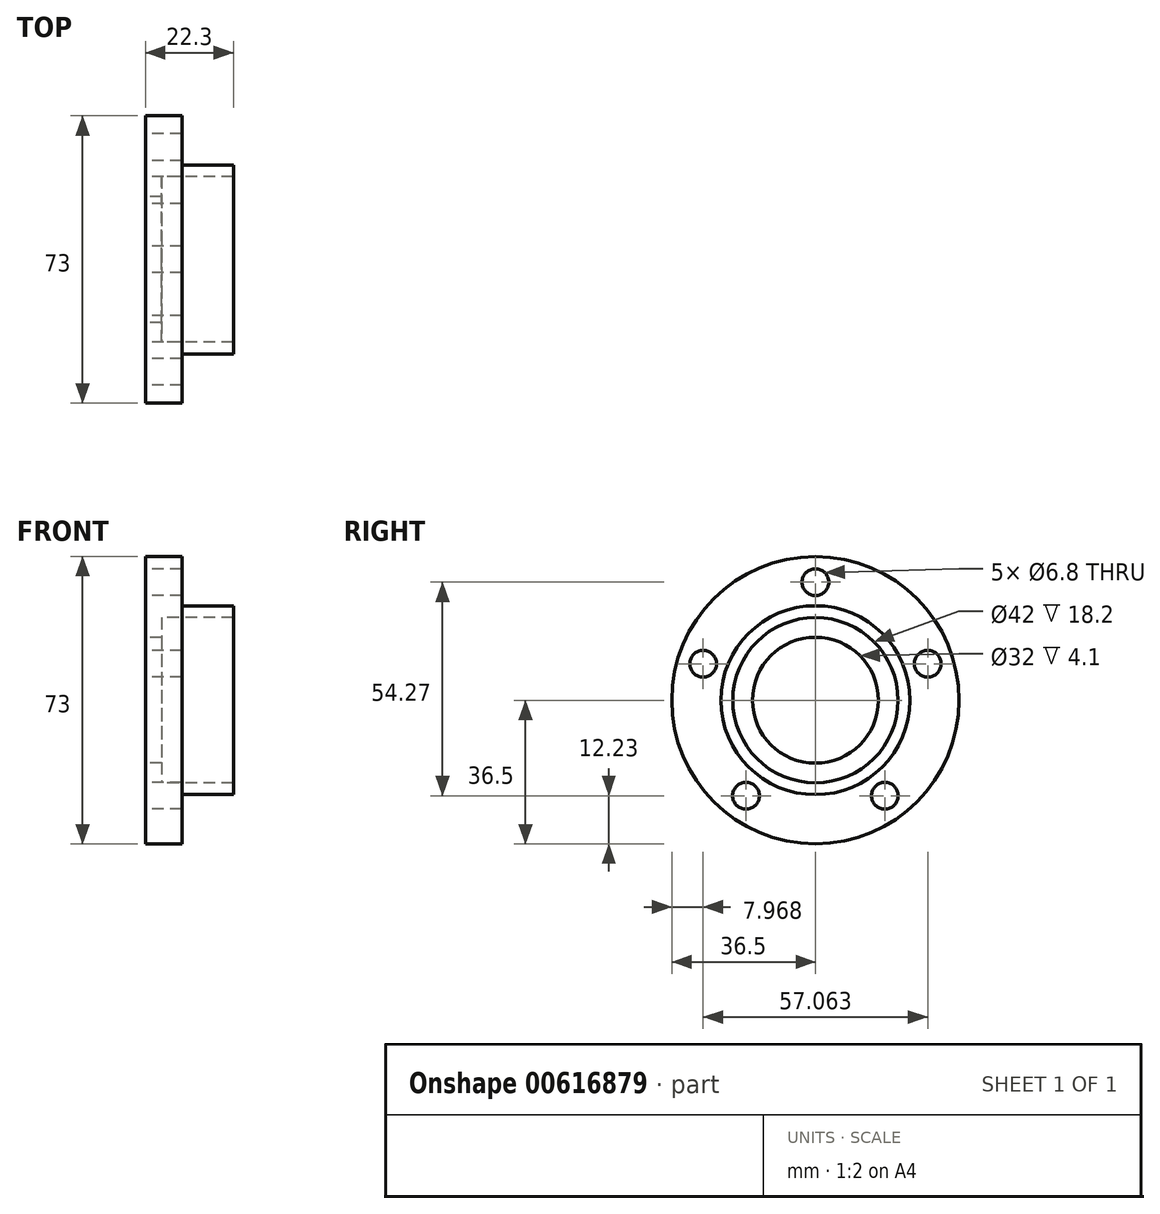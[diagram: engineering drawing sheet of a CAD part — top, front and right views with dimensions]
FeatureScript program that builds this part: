
annotation { "Feature Type Name" : "Feature", "Feature Type Description" : "" }
export const myFeature = defineFeature(function(context is Context, id is Id, definition is map)
    precondition{}
    {
        {
            var Q0;
            Q0=qCreatedBy(makeId("Front.planeOp"),FACE);
            var sketch = newSketch(context, id + "F0", { "sketchPlane" : qUnion([Q0])});
            skLineSegment(sketch, "E0", {"start": v(5.8, 21) * mm, "end": v(24, 21) * mm});
            skLineSegment(sketch, "E1", {"start": v(24, 24) * mm, "end": v(10.9, 24) * mm});
            skLineSegment(sketch, "E2", {"start": v(10.9, 24) * mm, "end": v(10.9, 36.5) * mm});
            skLineSegment(sketch, "E3", {"start": v(10.9, 36.5) * mm, "end": v(1.7, 36.5) * mm});
            skLineSegment(sketch, "E4", {"start": v(5.8, 21) * mm, "end": v(5.8, 16) * mm});
            skLineSegment(sketch, "E5", {"start": v(5.8, 16) * mm, "end": v(1.7, 16) * mm});
            skLineSegment(sketch, "E6", {"start": v(0, 0) * mm, "end": v(36.89, 0) * mm, "construction": true});
            skLineSegment(sketch, "E7", {"start": v(24, 21) * mm, "end": v(24, 24) * mm});
            skLineSegment(sketch, "E8", {"start": v(1.7, 16) * mm, "end": v(1.7, 36.5) * mm});
            skSolve(sketch);
        }
        {
            var Q0;
            Q0=makeQuery(id+"F0.imprint","IMPRINT",FACE,{"disambiguationData":[TD([[makeQuery(id+"F0.imprint","IMPRINT",EDGE,{"derivedFrom":sQuery(id+"F0.wireOp",EDGE,"E0")}),1.0]])]});
            var Q1;
            Q1=sQuery(id+"F0.wireOp",EDGE,"E6");
            revolve(context, id + "F1", {"surfaceOperationType" : NewSurfaceOperationType.NEW, "entities" : qUnion([Q0]), "axis" : qUnion([Q1]), "revolveType" : RevolveType.FULL});
        }
        {
            var Q0;
            Q0=makeQuery(id+"F1.opRevolve","SWEPT_FACE",FACE,{"disambiguationData":[OSD([sQuery(id+"F0.wireOp",EDGE,"E2")])]});
            var sketch = newSketch(context, id + "F2", { "sketchPlane" : qUnion([Q0])});
            skCircle(sketch, "E9.0", {"center": v(0, 0) * mm, "radius": 36.5 * mm, "construction": true});
            skCircle(sketch, "E10.0", {"center": v(0, 0) * mm, "radius": 24 * mm, "construction": true});
            skCircle(sketch, "E11", {"center": v(0, 0) * mm, "radius": 30 * mm, "construction": true});
            skCircle(sketch, "E12", {"center": v(0, 30) * mm, "radius": 2.5 * mm, "construction": true});
            skCircle(sketch, "E13.1.0", {"center": v(-28.53, 9.27) * mm, "radius": 2.5 * mm, "construction": true});
            skCircle(sketch, "E13.2.0", {"center": v(-17.63, -24.27) * mm, "radius": 2.5 * mm, "construction": true});
            skCircle(sketch, "E13.3.0", {"center": v(17.63, -24.27) * mm, "radius": 2.5 * mm, "construction": true});
            skCircle(sketch, "E13.4.0", {"center": v(28.53, 9.27) * mm, "radius": 2.5 * mm, "construction": true});
            skSolve(sketch);
        }
        {
            var Q0;
            Q0=sQuery(id+"F2.wireOp",VERTEX,"E12.center");
            var Q1;
            Q1=sQuery(id+"F2.wireOp",VERTEX,"E13.4.0.center");
            var Q2;
            Q2=sQuery(id+"F2.wireOp",VERTEX,"E13.3.0.center");
            var Q3;
            Q3=sQuery(id+"F2.wireOp",VERTEX,"E13.2.0.center");
            var Q4;
            Q4=sQuery(id+"F2.wireOp",VERTEX,"E13.1.0.center");
            var Q5;
            Q5=makeQuery(id+"F1.opRevolve","SWEPT_BODY",BODY,{"disambiguationData":[OSD([sQuery(id+"F0.wireOp",EDGE,"E0"),sQuery(id+"F0.wireOp",EDGE,"OTkLGTA6-KaCv-k9Gx-gSGP-BNMddn67J8YU"),sQuery(id+"F0.wireOp",EDGE,"E1"),sQuery(id+"F0.wireOp",EDGE,"dEY0dlj1-HALh-Q35b-Qvuc-SWXWftyWZpDn"),sQuery(id+"F0.wireOp",EDGE,"E2"),sQuery(id+"F0.wireOp",EDGE,"E3"),sQuery(id+"F0.wireOp",EDGE,"qeZPi9Dx-MjPP-eJMO-PXdc-L6tLdkU5ELdf"),sQuery(id+"F0.wireOp",EDGE,"E4"),sQuery(id+"F0.wireOp",EDGE,"E5"),sQuery(id+"F0.wireOp",EDGE,"CKjobQbc-QJ0u-P1ni-fmlm-5WQ4OysDmLDC")])]});
            hole(context, id + "F3", {"style" : HoleStyle.SIMPLE, "endStyle" : HoleEndStyle.BLIND, "standardTappedOrClearance" : lookupTablePath({ "standard" : "ISO", "engagement" : "75%", "pitch" : "1.25 mm", "size" : "M8", "type" : "Tapped" }), "standardBlindInLast" : lookupTablePath({ "standard" : "ISO", "engagement" : "75%", "pitch" : "1.25 mm", "size" : "M8", "type" : "Tapped" }), "holeDiameter" : 6.8 * mm, "majorDiameter" : 8 * mm, "showTappedDepth" : true, "holeDepth" : 48.75 * mm, "isTappedThrough" : true, "tappedDepth" : 45 * mm, "tapClearance" : 3, "locations" : qUnion([Q0, Q1, Q2, Q3, Q4]), "scope" : qUnion([Q5]), "startStyle" : HoleStartStyle.PART});
        }
    });
